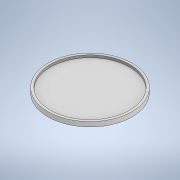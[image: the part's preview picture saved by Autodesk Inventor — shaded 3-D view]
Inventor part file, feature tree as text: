
AUTODESK INVENTOR PART (.ipt)
format: ipt  version: 2022 (Build 260153000, 153)  size: 114,176 bytes
history: native  units: in
note: dims shown in document units (in); Inventor stores cm internally (conversion verified against a paired STEP export)
features: extrude x3, sketch x1
ambient origin geometry x8: Origin, YZ Plane, XZ Plane, XY Plane, X Axis, Y Axis, Z Axis, Center Point
bodies: Solid1 (feature_tree)
feature tree (4):
  sketch  "Sketch1"  dims[d0=9.0in d1=0.25in d2=5.0in d3=5.0in d4=0.25in d5=0.25in d6=0.0in d7=0.5in d8=0.0in d9=0.25in d10=0.0in]
  extrude  "Extrusion1"  Depth=0.25in
  extrude  "Extrusion2"  Depth=0.25in
  extrude  "Extrusion3"  Depth=0.25in
